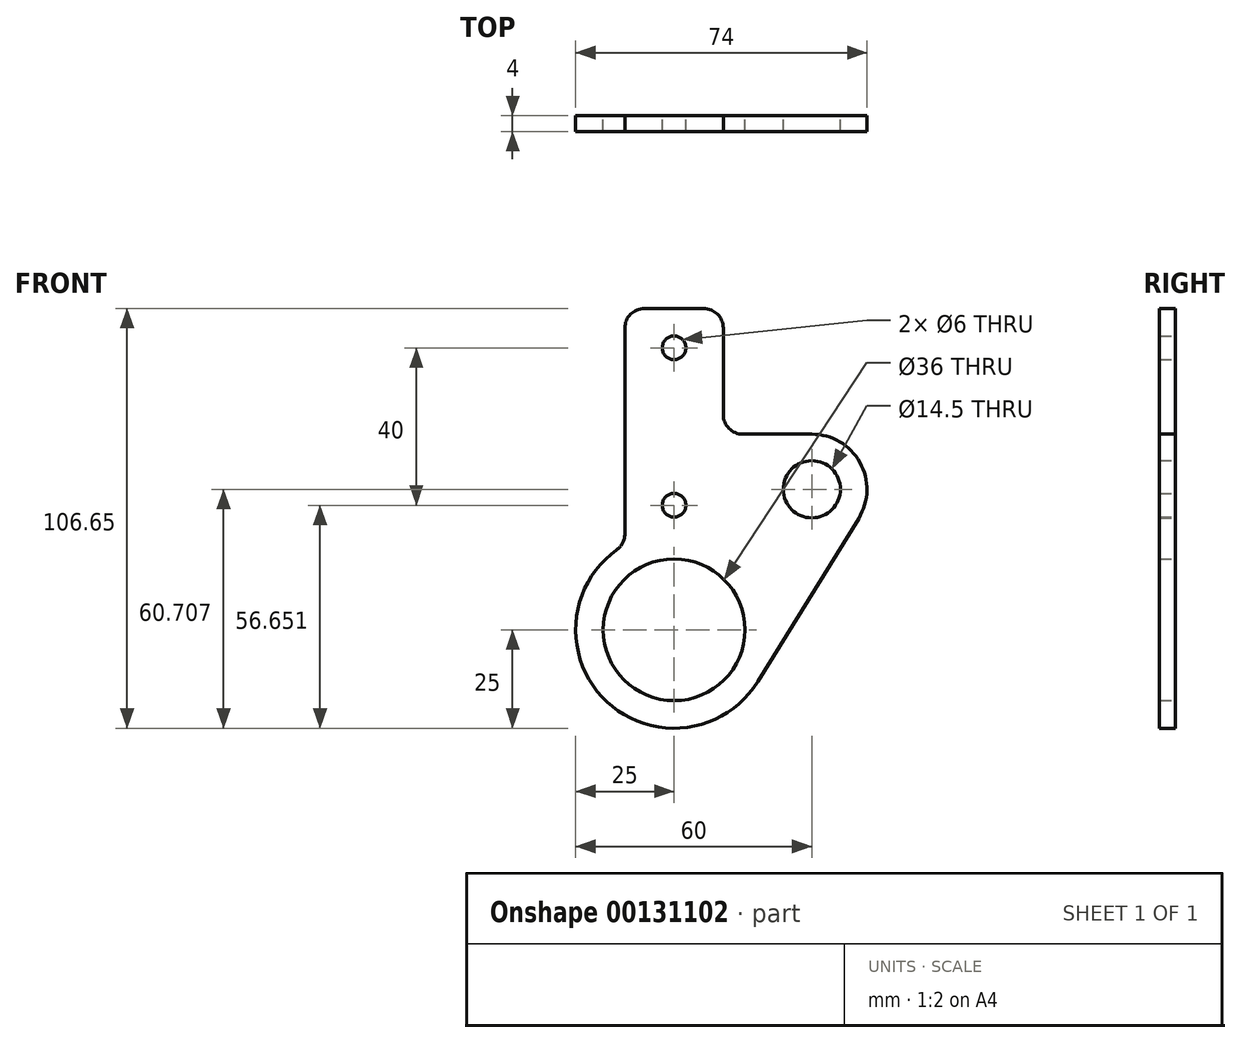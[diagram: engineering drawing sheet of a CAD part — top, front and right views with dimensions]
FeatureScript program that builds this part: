
annotation { "Feature Type Name" : "Feature", "Feature Type Description" : "" }
export const myFeature = defineFeature(function(context is Context, id is Id, definition is map)
    precondition{}
    {
        {
            var Q0;
            Q0=qCreatedBy(makeId("Front.planeOp"),FACE);
            var sketch = newSketch(context, id + "F0", { "sketchPlane" : qUnion([Q0])});
            skCircle(sketch, "E0", {"center": v(0, 0) * mm, "radius": 18 * mm});
            skArc(sketch, "E1", {"start": v(-12.5, 21.65) * mm, "mid": v(0, -25) * mm, "end": v(12.5, 21.65) * mm});
            skLineSegment(sketch, "E2.bottom", {"start": v(12.5, 21.65) * mm, "end": v(-12.5, 21.65) * mm, "construction": true});
            skLineSegment(sketch, "E2.top", {"start": v(12.5, 81.65) * mm, "end": v(-12.5, 81.65) * mm});
            skLineSegment(sketch, "E2.left", {"start": v(12.5, 21.65) * mm, "end": v(12.5, 81.65) * mm});
            skLineSegment(sketch, "E2.right", {"start": v(-12.5, 21.65) * mm, "end": v(-12.5, 81.65) * mm});
            skPoint(sketch, "E3", {"position": v(0, 31.65) * mm});
            skPoint(sketch, "E3.positionSnap0", {"position": v(0, 21.65) * mm});
            skPoint(sketch, "E4", {"position": v(0, 71.65) * mm});
            skPoint(sketch, "E5", {"position": v(35, 35.7) * mm});
            skCircle(sketch, "E6", {"center": v(35, 35.7) * mm, "radius": 14 * mm});
            skLineSegment(sketch, "E7", {"start": v(21.27, -13.14) * mm, "end": v(46.9, 28.35) * mm});
            skLineSegment(sketch, "E8", {"start": v(35, 49.7) * mm, "end": v(12.5, 49.7) * mm});
            skSolve(sketch);
        }
        {
            var Q0;
            Q0=makeQuery(id+"F0.imprint","IMPRINT",FACE,{"disambiguationData":[TD([[makeQuery(id+"F0.imprint","IMPRINT",EDGE,{"derivedFrom":sQuery(id+"F0.wireOp",EDGE,"E0")}),-1.0]])]});
            var Q1;
            {var subQ0=sQuery(id+"F0.wireOp",EDGE,"E7");Q1=makeQuery(id+"F0.imprint","IMPRINT",FACE,{"disambiguationData":[TD([[makeQuery(id+"F0.imprint","IMPRINT",EDGE,{"derivedFrom":subQ0}),1.0]])]});}
            var Q2;
            {var subQ0=sQuery(id+"F0.wireOp",EDGE,"E6");var subQ1=makeQuery(id+"F0.imprint","INTERSECT",VERTEX,{"derivedFrom":[subQ0,sQuery(id+"F0.wireOp",EDGE,"E7")]});Q2=makeQuery(id+"F0.imprint","IMPRINT",FACE,{"disambiguationData":[TD([[makeQuery(id+"F0.imprint","IMPRINT",EDGE,{"disambiguationData":[TD([[subQ1,1.0]])],"derivedFrom":subQ0}),1.0]])]});}
            extrude(context, id + "F1", {"entities" : qUnion([Q0, Q1, Q2]), "depth" : 4 * mm});
        }
        {
            var Q0;
            Q0=makeQuery(id+"F1.opExtrude","SWEPT_EDGE",EDGE,{"disambiguationData":[OSD([sQuery(id+"F0.wireOp",EDGE,"E2.top"),sQuery(id+"F0.wireOp",EDGE,"E2.left")])]});
            var Q1;
            Q1=makeQuery(id+"F1.opExtrude","SWEPT_EDGE",EDGE,{"disambiguationData":[OSD([sQuery(id+"F0.wireOp",EDGE,"E1"),sQuery(id+"F0.wireOp",EDGE,"E2.left")])]});
            var Q2;
            Q2=makeQuery(id+"F1.opExtrude","SWEPT_EDGE",EDGE,{"disambiguationData":[OSD([sQuery(id+"F0.wireOp",EDGE,"E1"),sQuery(id+"F0.wireOp",EDGE,"E2.right")])]});
            var Q3;
            Q3=makeQuery(id+"F1.opExtrude","SWEPT_EDGE",EDGE,{"disambiguationData":[OSD([sQuery(id+"F0.wireOp",EDGE,"E2.top"),sQuery(id+"F0.wireOp",EDGE,"E2.right")])]});
            fillet(context, id + "F2", {"entities" : qUnion([Q0, Q1, Q2, Q3]), "radius" : 5 * mm, "tangentPropagation" : true, "allowEdgeOverflow" : false});
        }
        {
            var Q0;
            Q0=sQuery(id+"F0.wireOp",VERTEX,"E3");
            var Q1;
            Q1=sQuery(id+"F0.wireOp",VERTEX,"E4");
            var Q2;
            Q2=makeQuery(id+"F1.opExtrude","SWEPT_BODY",BODY,{"disambiguationData":[OSD([sQuery(id+"F0.wireOp",EDGE,"E0"),sQuery(id+"F0.wireOp",EDGE,"E1"),sQuery(id+"F0.wireOp",EDGE,"E2.top"),sQuery(id+"F0.wireOp",EDGE,"E2.left"),sQuery(id+"F0.wireOp",EDGE,"E2.right")])]});
            hole(context, id + "F3", {"style" : HoleStyle.SIMPLE, "endStyle" : HoleEndStyle.THROUGH, "oppositeDirection" : true, "holeDiameter" : 6 * mm, "locations" : qUnion([Q0, Q1]), "scope" : qUnion([Q2]), "isTappedThrough" : true});
        }
        {
            var Q0;
            Q0=sQuery(id+"F0.wireOp",VERTEX,"E5");
            var Q1;
            Q1=makeQuery(id+"F1.opExtrude","SWEPT_BODY",BODY,{"disambiguationData":[OSD([sQuery(id+"F0.wireOp",EDGE,"E0"),sQuery(id+"F0.wireOp",EDGE,"E1"),sQuery(id+"F0.wireOp",EDGE,"E2.top"),sQuery(id+"F0.wireOp",EDGE,"E2.left"),sQuery(id+"F0.wireOp",EDGE,"E2.right"),sQuery(id+"F0.wireOp",EDGE,"E6"),sQuery(id+"F0.wireOp",EDGE,"E7"),sQuery(id+"F0.wireOp",EDGE,"E8")])]});
            hole(context, id + "F4", {"style" : HoleStyle.SIMPLE, "endStyle" : HoleEndStyle.THROUGH, "oppositeDirection" : true, "holeDiameter" : 14.5 * mm, "locations" : qUnion([Q0]), "scope" : qUnion([Q1]), "isTappedThrough" : true});
        }
    });
